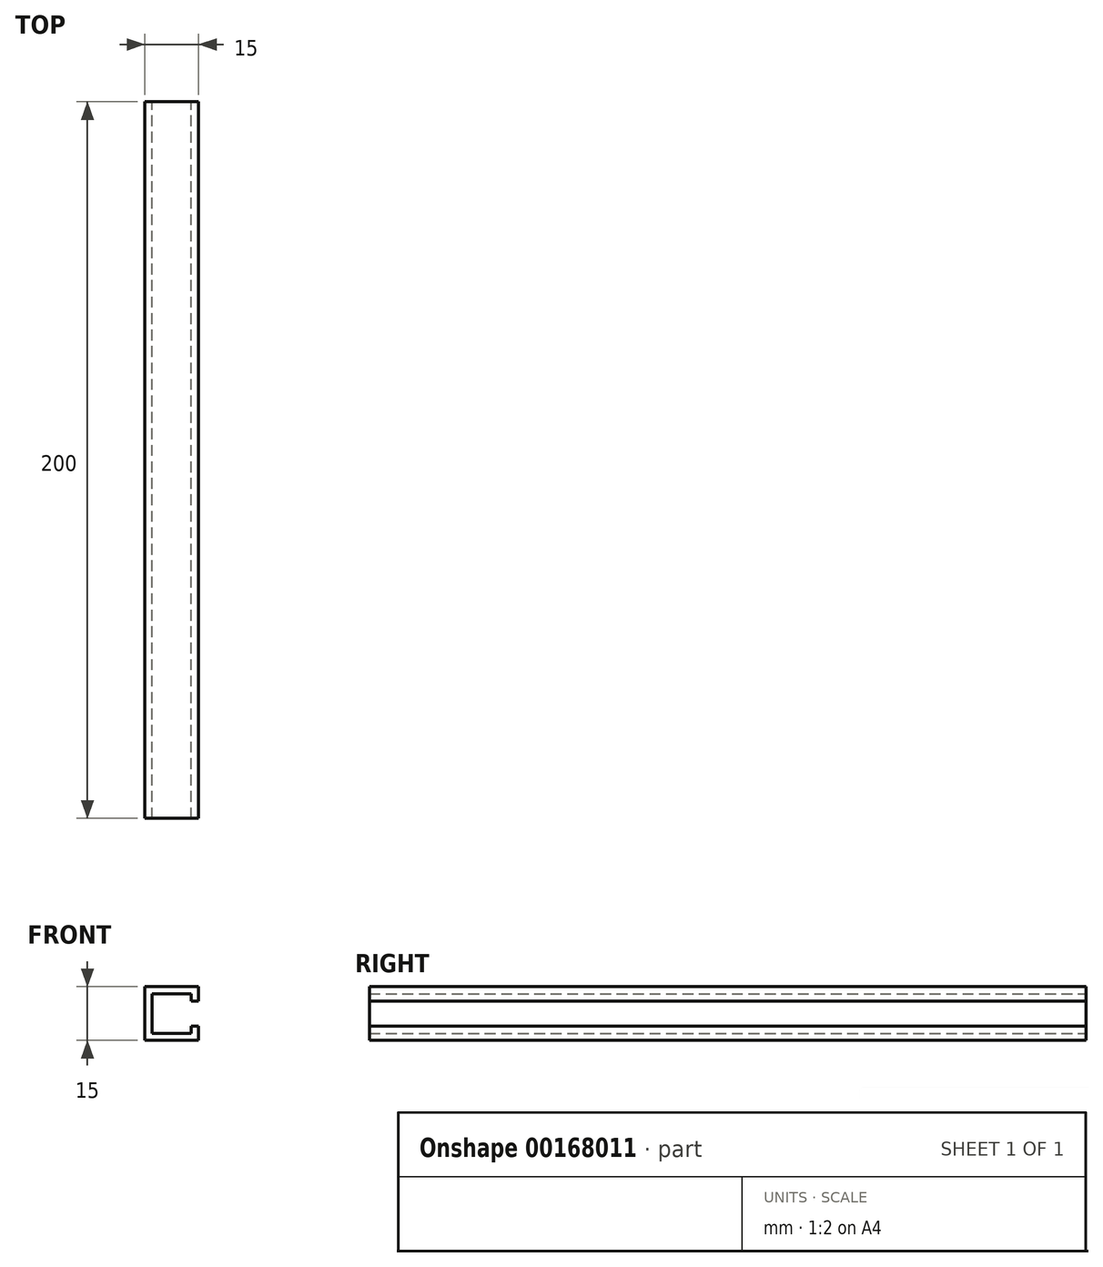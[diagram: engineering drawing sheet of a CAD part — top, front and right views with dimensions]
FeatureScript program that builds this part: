
annotation { "Feature Type Name" : "Feature", "Feature Type Description" : "" }
export const myFeature = defineFeature(function(context is Context, id is Id, definition is map)
    precondition{}
    {
        {
            var Q0;
            Q0=qCreatedBy(makeId("Front.planeOp"),FACE);
            var sketch = newSketch(context, id + "F0", { "sketchPlane" : qUnion([Q0])});
            skLineSegment(sketch, "E0.bottom", {"start": v(7.5, 7.5) * mm, "end": v(-7.5, 7.5) * mm});
            skLineSegment(sketch, "E0.top", {"start": v(7.5, -7.5) * mm, "end": v(-7.5, -7.5) * mm});
            skLineSegment(sketch, "E0.right", {"start": v(-7.5, 7.5) * mm, "end": v(-7.5, -7.5) * mm});
            skPoint(sketch, "E0.middle", {"position": v(0, 0) * mm});
            skLineSegment(sketch, "E1.0", {"start": v(5.5, -5.5) * mm, "end": v(-5.5, -5.5) * mm});
            skLineSegment(sketch, "E1.1", {"start": v(-5.5, 5.5) * mm, "end": v(-5.5, -5.5) * mm});
            skLineSegment(sketch, "E1.2", {"start": v(5.5, 5.5) * mm, "end": v(-5.5, 5.5) * mm});
            skLineSegment(sketch, "E2", {"start": v(7.5, 3.5) * mm, "end": v(5.5, 3.5) * mm});
            skLineSegment(sketch, "E3", {"start": v(5.5, 3.5) * mm, "end": v(5.5, 5.5) * mm});
            skLineSegment(sketch, "E4", {"start": v(7.5, 3.5) * mm, "end": v(7.5, 7.5) * mm});
            skLineSegment(sketch, "E5.MirrorCS", {"start": v(5.5, -3.5) * mm, "end": v(5.5, -5.5) * mm});
            skLineSegment(sketch, "E6.MirrorCS", {"start": v(7.5, -3.5) * mm, "end": v(7.5, -7.5) * mm});
            skLineSegment(sketch, "E7.MirrorCS", {"start": v(7.5, -3.5) * mm, "end": v(5.5, -3.5) * mm});
            skSolve(sketch);
        }
        {
            var Q0;
            Q0 = qSketchRegion(id + "F0", true);
            extrude(context, id + "F1", {"entities" : qUnion([Q0]), "depth" : 200 * mm, "symmetric" : true});
        }
    });
